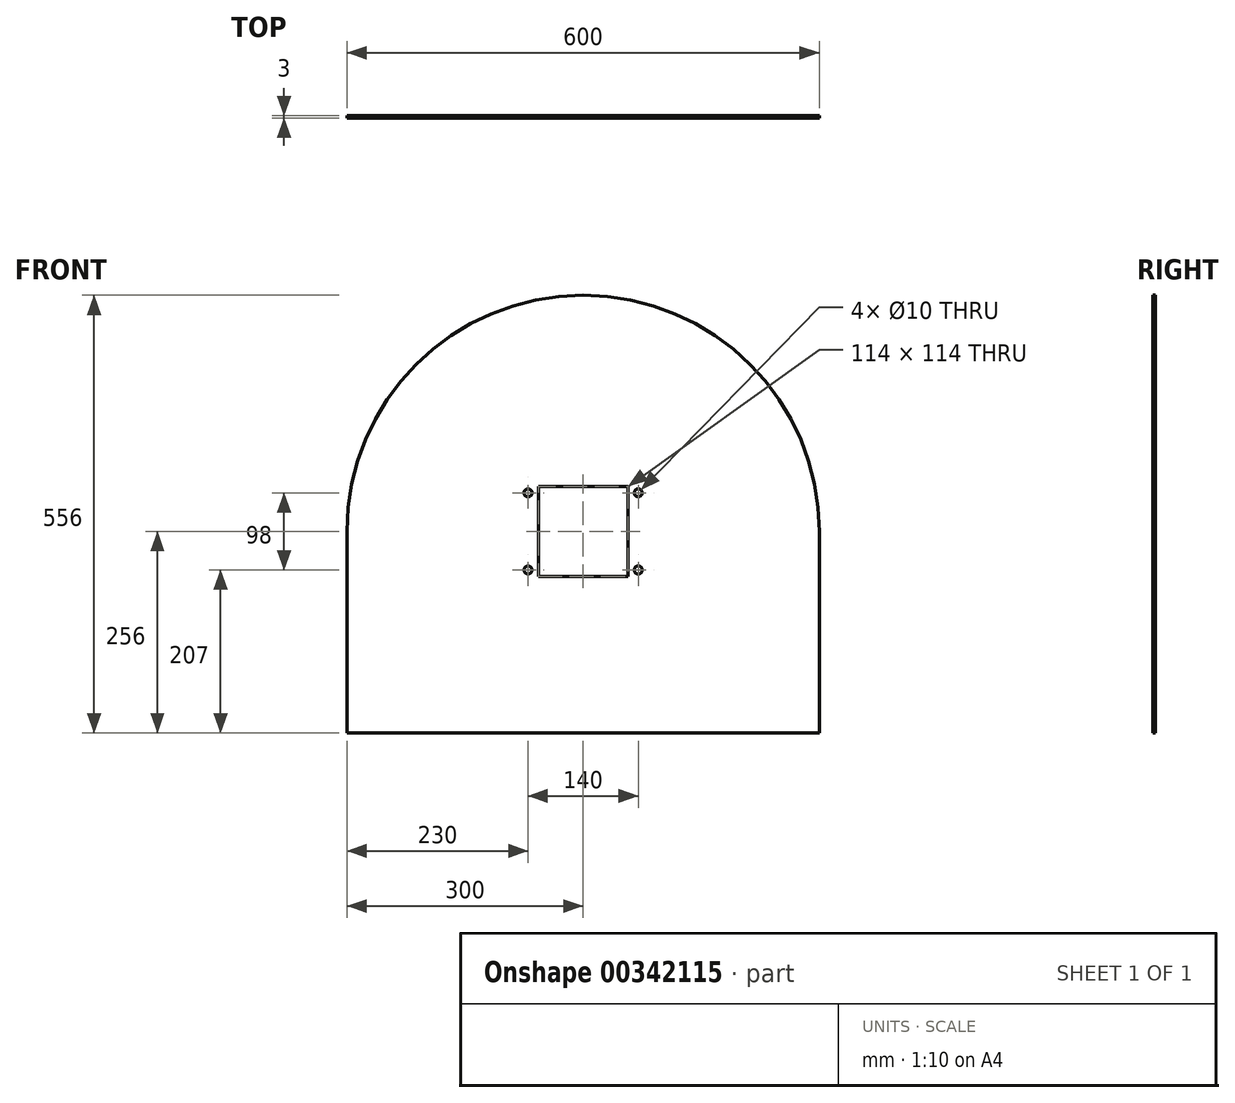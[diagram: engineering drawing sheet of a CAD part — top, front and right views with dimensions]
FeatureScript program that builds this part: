
annotation { "Feature Type Name" : "Feature", "Feature Type Description" : "" }
export const myFeature = defineFeature(function(context is Context, id is Id, definition is map)
    precondition{}
    {
        {
            var Q0;
            Q0=qCreatedBy(makeId("Front.planeOp"),FACE);
            var sketch = newSketch(context, id + "F0", { "sketchPlane" : qUnion([Q0])});
            skLineSegment(sketch, "E0.bottom", {"start": v(-300, -128) * mm, "end": v(300, -128) * mm});
            skLineSegment(sketch, "E0.top", {"start": v(-300, 128) * mm, "end": v(300, 128) * mm});
            skLineSegment(sketch, "E0.left", {"start": v(-300, -128) * mm, "end": v(-300, 128) * mm});
            skLineSegment(sketch, "E0.right", {"start": v(300, -128) * mm, "end": v(300, 128) * mm});
            skPoint(sketch, "E0.middle", {"position": v(0, 0) * mm});
            skPoint(sketch, "E1.endSnap0", {"position": v(0, 128) * mm});
            skArc(sketch, "E2", {"start": v(300, 128) * mm, "mid": v(0, 428) * mm, "end": v(-300, 128) * mm});
            skLineSegment(sketch, "E3.bottom", {"start": v(-57, 71) * mm, "end": v(57, 71) * mm});
            skLineSegment(sketch, "E3.top", {"start": v(-57, 185) * mm, "end": v(57, 185) * mm});
            skLineSegment(sketch, "E3.left", {"start": v(-57, 71) * mm, "end": v(-57, 185) * mm});
            skLineSegment(sketch, "E3.right", {"start": v(57, 71) * mm, "end": v(57, 185) * mm});
            skPoint(sketch, "E4.endSnap0", {"position": v(0, 185) * mm});
            skLineSegment(sketch, "E5", {"start": v(0, 177) * mm, "end": v(70, 177) * mm});
            skLineSegment(sketch, "E6", {"start": v(0, 177) * mm, "end": v(-70, 177) * mm});
            skPoint(sketch, "E7.endSnap0", {"position": v(0, 71) * mm});
            skLineSegment(sketch, "E8", {"start": v(0, 79) * mm, "end": v(70, 79) * mm});
            skLineSegment(sketch, "E9", {"start": v(0, 79) * mm, "end": v(-70, 79) * mm});
            skLineSegment(sketch, "E10", {"start": v(0, 128) * mm, "end": v(0, 79) * mm});
            skLineSegment(sketch, "E11", {"start": v(0, 128) * mm, "end": v(0, 177) * mm});
            skCircle(sketch, "E12", {"center": v(70, 79) * mm, "radius": 5 * mm});
            skCircle(sketch, "E13", {"center": v(70, 177) * mm, "radius": 5 * mm});
            skCircle(sketch, "E14", {"center": v(-70, 177) * mm, "radius": 5 * mm});
            skCircle(sketch, "E15", {"center": v(-70, 79) * mm, "radius": 5 * mm});
            skSolve(sketch);
        }
        {
            var Q0;
            Q0=qSketchRegion(id+"F0",true);
            extrude(context, id + "F1", {"entities" : qUnion([Q0]), "depth" : 3 * mm});
        }
    });
